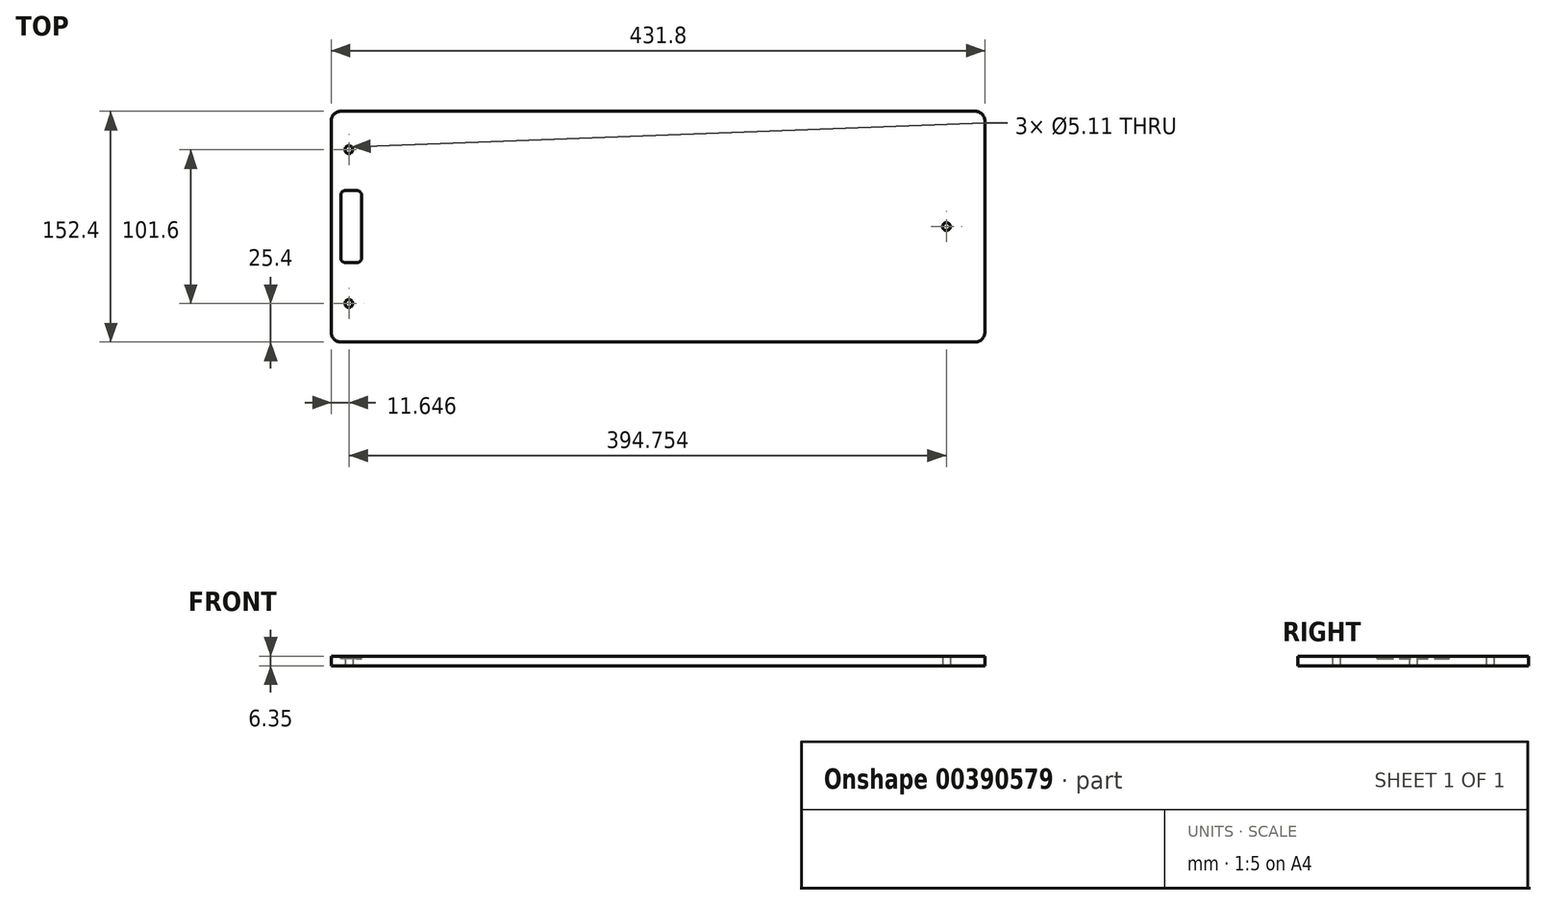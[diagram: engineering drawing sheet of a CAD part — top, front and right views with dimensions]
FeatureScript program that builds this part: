
annotation { "Feature Type Name" : "Feature", "Feature Type Description" : "" }
export const myFeature = defineFeature(function(context is Context, id is Id, definition is map)
    precondition{}
    {
        {
            var Q0;
            Q0=qCreatedBy(makeId("Top.planeOp"),FACE);
            var sketch = newSketch(context, id + "F0", { "sketchPlane" : qUnion([Q0])});
            skLineSegment(sketch, "E0.bottom", {"start": v(215.9, -76.2) * mm, "end": v(-215.9, -76.2) * mm});
            skLineSegment(sketch, "E0.top", {"start": v(215.9, 76.2) * mm, "end": v(-215.9, 76.2) * mm});
            skLineSegment(sketch, "E0.left", {"start": v(215.9, -76.2) * mm, "end": v(215.9, 76.2) * mm});
            skLineSegment(sketch, "E0.right", {"start": v(-215.9, -76.2) * mm, "end": v(-215.9, 76.2) * mm});
            skPoint(sketch, "E0.middle", {"position": v(0, 0) * mm});
            skCircle(sketch, "E1", {"center": v(190.5, 0) * mm, "radius": 2.55 * mm});
            skCircle(sketch, "E2", {"center": v(-204.25, -50.8) * mm, "radius": 2.55 * mm});
            skCircle(sketch, "E3", {"center": v(-204.25, 50.8) * mm, "radius": 2.55 * mm});
            skSolve(sketch);
        }
        {
            var Q0;
            Q0 = qSketchRegion(id + "F0", true);
            extrude(context, id + "F1", {"entities" : qUnion([Q0]), "depth" : 6.35 * mm});
        }
        {
            var Q0;
            Q0=makeQuery(id+"F1.opExtrude","CAP_FACE",FACE,{"disambiguationData":[OSD([sQuery(id+"F0.wireOp",EDGE,"E0.bottom"),sQuery(id+"F0.wireOp",EDGE,"E0.top"),sQuery(id+"F0.wireOp",EDGE,"E0.left"),sQuery(id+"F0.wireOp",EDGE,"E0.right"),sQuery(id+"F0.wireOp",EDGE,"E1"),sQuery(id+"F0.wireOp",EDGE,"E2"),sQuery(id+"F0.wireOp",EDGE,"E3")])],"isStart":false});
            var sketch = newSketch(context, id + "F2", { "sketchPlane" : qUnion([Q0])});
            skLineSegment(sketch, "E4.bottom", {"start": v(-195.86, -23.82) * mm, "end": v(-209.66, -23.82) * mm});
            skLineSegment(sketch, "E4.top", {"start": v(-195.86, 23.82) * mm, "end": v(-209.66, 23.82) * mm});
            skLineSegment(sketch, "E4.left", {"start": v(-195.86, -23.82) * mm, "end": v(-195.86, 23.82) * mm});
            skLineSegment(sketch, "E4.right", {"start": v(-209.66, -23.82) * mm, "end": v(-209.66, 23.82) * mm});
            skPoint(sketch, "E4.middle", {"position": v(-202.76, 0) * mm});
            skSolve(sketch);
        }
        {
            var Q0;
            Q0 = qSketchRegion(id + "F2", true);
            extrude(context, id + "F3", {"entities" : qUnion([Q0]), "operationType" : NewBodyOperationType.REMOVE, "oppositeDirection" : true, "depth" : 1.59 * mm});
        }
        {
            var Q0;
            Q0=makeQuery(id+"F3.boolean.opBoolean","COPY",EDGE,{"derivedFrom":makeQuery(id+"F3.opExtrude","SWEPT_EDGE",EDGE,{"disambiguationData":[OSD([sQuery(id+"F2.wireOp",EDGE,"E4.top"),sQuery(id+"F2.wireOp",EDGE,"E4.right")])]})});
            var Q1;
            Q1=makeQuery(id+"F3.boolean.opBoolean","COPY",EDGE,{"derivedFrom":makeQuery(id+"F3.opExtrude","SWEPT_EDGE",EDGE,{"disambiguationData":[OSD([sQuery(id+"F2.wireOp",EDGE,"E4.top"),sQuery(id+"F2.wireOp",EDGE,"E4.left")])]})});
            var Q2;
            Q2=makeQuery(id+"F3.boolean.opBoolean","COPY",EDGE,{"derivedFrom":makeQuery(id+"F3.opExtrude","SWEPT_EDGE",EDGE,{"disambiguationData":[OSD([sQuery(id+"F2.wireOp",EDGE,"E4.bottom"),sQuery(id+"F2.wireOp",EDGE,"E4.right")])]})});
            var Q3;
            Q3=makeQuery(id+"F3.boolean.opBoolean","COPY",EDGE,{"derivedFrom":makeQuery(id+"F3.opExtrude","SWEPT_EDGE",EDGE,{"disambiguationData":[OSD([sQuery(id+"F2.wireOp",EDGE,"E4.bottom"),sQuery(id+"F2.wireOp",EDGE,"E4.left")])]})});
            fillet(context, id + "F4", {"entities" : qUnion([Q0, Q1, Q2, Q3]), "radius" : 3.17 * mm, "tangentPropagation" : true, "allowEdgeOverflow" : false});
        }
        {
            var Q0;
            Q0=makeQuery(id+"F1.opExtrude","SWEPT_EDGE",EDGE,{"disambiguationData":[OSD([sQuery(id+"F0.wireOp",EDGE,"E0.bottom"),sQuery(id+"F0.wireOp",EDGE,"E0.right")])]});
            var Q1;
            Q1=makeQuery(id+"F1.opExtrude","SWEPT_EDGE",EDGE,{"disambiguationData":[OSD([sQuery(id+"F0.wireOp",EDGE,"E0.top"),sQuery(id+"F0.wireOp",EDGE,"E0.right")])]});
            var Q2;
            Q2=makeQuery(id+"F1.opExtrude","SWEPT_EDGE",EDGE,{"disambiguationData":[OSD([sQuery(id+"F0.wireOp",EDGE,"E0.top"),sQuery(id+"F0.wireOp",EDGE,"E0.left")])]});
            var Q3;
            Q3=makeQuery(id+"F1.opExtrude","SWEPT_EDGE",EDGE,{"disambiguationData":[OSD([sQuery(id+"F0.wireOp",EDGE,"E0.bottom"),sQuery(id+"F0.wireOp",EDGE,"E0.left")])]});
            fillet(context, id + "F5", {"entities" : qUnion([Q0, Q1, Q2, Q3]), "radius" : 6.35 * mm, "tangentPropagation" : true, "allowEdgeOverflow" : false});
        }
    });
